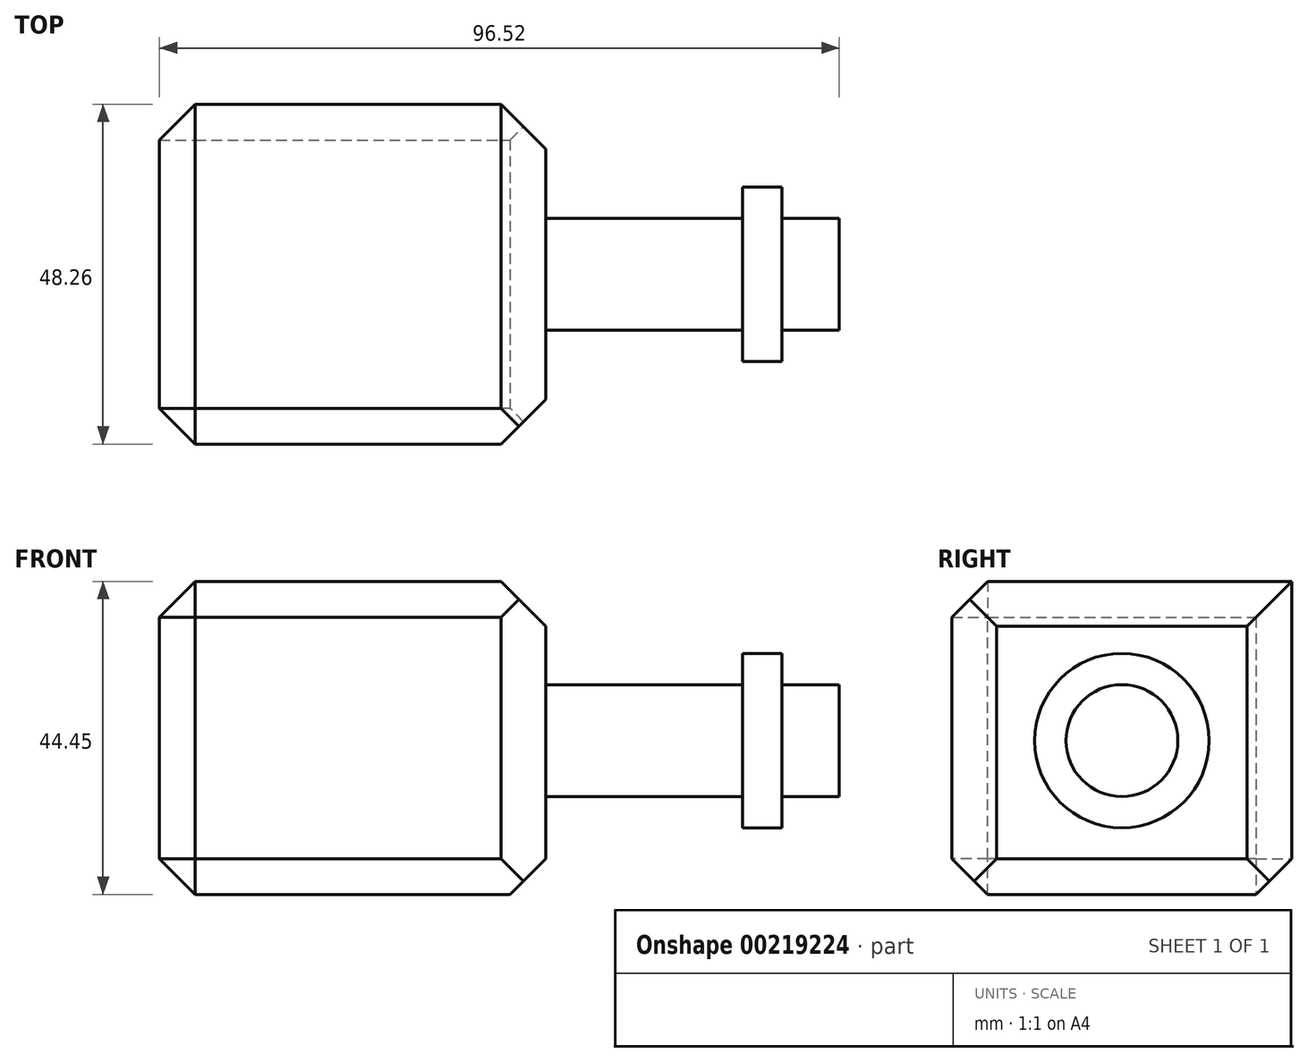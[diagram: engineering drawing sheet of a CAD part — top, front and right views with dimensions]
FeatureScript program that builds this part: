
annotation { "Feature Type Name" : "Feature", "Feature Type Description" : "" }
export const myFeature = defineFeature(function(context is Context, id is Id, definition is map)
    precondition{}
    {
        {
            var Q0;
            Q0=qCreatedBy(makeId("Top.planeOp"),FACE);
            var sketch = newSketch(context, id + "F0", { "sketchPlane" : qUnion([Q0])});
            skLineSegment(sketch, "E0.bottom", {"start": v(-122.1, 35.47) * mm, "end": v(-67.24, 35.47) * mm});
            skLineSegment(sketch, "E0.top", {"start": v(-122.1, -12.8) * mm, "end": v(-67.24, -12.8) * mm});
            skLineSegment(sketch, "E0.left", {"start": v(-122.1, 35.47) * mm, "end": v(-122.1, -12.8) * mm});
            skLineSegment(sketch, "E0.right", {"start": v(-67.24, 35.47) * mm, "end": v(-67.24, -12.8) * mm});
            skSolve(sketch);
        }
        {
            var Q0;
            Q0=makeQuery(id+"F0.imprint","IMPRINT",FACE,{"disambiguationData":[TD([[makeQuery(id+"F0.imprint","IMPRINT",EDGE,{"derivedFrom":sQuery(id+"F0.wireOp",EDGE,"E0.bottom")}),-1.0]])]});
            extrude(context, id + "F1", {"entities" : qUnion([Q0]), "depth" : 44.45 * mm});
        }
        {
            var Q0;
            Q0=makeQuery(id+"F1.opExtrude","SWEPT_FACE",FACE,{"disambiguationData":[OSD([sQuery(id+"F0.wireOp",EDGE,"E0.right")])]});
            var sketch = newSketch(context, id + "F2", { "sketchPlane" : qUnion([Q0])});
            skCircle(sketch, "E1", {"center": v(11.34, 21.84) * mm, "radius": 7.94 * mm});
            skCircle(sketch, "E2", {"center": v(11.34, 21.84) * mm, "radius": 12.39 * mm});
            skSolve(sketch);
        }
        {
            var Q0;
            Q0=makeQuery(id+"F2.imprint","IMPRINT",FACE,{"disambiguationData":[TD([[makeQuery(id+"F2.imprint","IMPRINT",EDGE,{"derivedFrom":sQuery(id+"F2.wireOp",EDGE,"E1")}),1.0]])]});
            extrude(context, id + "F3", {"entities" : qUnion([Q0]), "operationType" : NewBodyOperationType.ADD, "depth" : 41.66 * mm});
        }
        {
            var Q0;
            Q0=makeQuery(id+"F2.imprint","IMPRINT",FACE,{"disambiguationData":[TD([[makeQuery(id+"F2.imprint","IMPRINT",EDGE,{"derivedFrom":sQuery(id+"F2.wireOp",EDGE,"E1")}),-1.0]])]});
            extrude(context, id + "F4", {"entities" : qUnion([Q0]), "operationType" : NewBodyOperationType.ADD, "depth" : 33.53 * mm});
        }
        {
            var Q0;
            Q0=makeQuery(id+"F1.opExtrude","CAP_FACE",FACE,{"disambiguationData":[OSD([sQuery(id+"F0.wireOp",EDGE,"E0.bottom"),sQuery(id+"F0.wireOp",EDGE,"E0.top"),sQuery(id+"F0.wireOp",EDGE,"E0.left"),sQuery(id+"F0.wireOp",EDGE,"E0.right")])],"isStart":false});
            extrude(context, id + "F5", {"entities" : qUnion([Q0]), "operationType" : NewBodyOperationType.REMOVE, "oppositeDirection" : true, "depth" : 36.83 * mm});
        }
        {
            var Q0;
            Q0=makeQuery(id+"F2.imprint","IMPRINT",FACE,{"disambiguationData":[TD([[makeQuery(id+"F2.imprint","IMPRINT",EDGE,{"derivedFrom":sQuery(id+"F2.wireOp",EDGE,"E1")}),-1.0]])]});
            extrude(context, id + "F6", {"entities" : qUnion([Q0]), "operationType" : NewBodyOperationType.REMOVE, "depth" : 27.94 * mm});
        }
        {
            var Q0;
            Q0=makeQuery(id+"F2.imprint","IMPRINT",FACE,{"disambiguationData":[TD([[makeQuery(id+"F2.imprint","IMPRINT",EDGE,{"derivedFrom":sQuery(id+"F2.wireOp",EDGE,"E2")}),-1.0]])]});
            var Q1;
            Q1=makeQuery(id+"F1.opExtrude","SWEPT_FACE",FACE,{"disambiguationData":[OSD([sQuery(id+"F0.wireOp",EDGE,"E0.left")])]});
            extrude(context, id + "F7", {"entities" : qUnion([Q0]), "operationType" : NewBodyOperationType.ADD, "endBound" : BoundingType.UP_TO_SURFACE, "oppositeDirection" : true, "endBoundEntityFace" : qUnion([Q1]), "depth" : 49.02 * mm});
        }
        {
            var Q0;
            Q0=makeQuery(id+"F2.imprint","IMPRINT",FACE,{"disambiguationData":[TD([[makeQuery(id+"F2.imprint","IMPRINT",EDGE,{"derivedFrom":sQuery(id+"F2.wireOp",EDGE,"E1")}),1.0]])]});
            var Q1;
            Q1=makeQuery(id+"F2.imprint","IMPRINT",FACE,{"disambiguationData":[TD([[makeQuery(id+"F2.imprint","IMPRINT",EDGE,{"derivedFrom":sQuery(id+"F2.wireOp",EDGE,"E1")}),-1.0]])]});
            var Q2;
            Q2=makeQuery(id+"F7.boolean.opBoolean","MERGE",FACE,{"derivedFrom":[makeQuery(id+"F1.opExtrude","SWEPT_FACE",FACE,{"disambiguationData":[OSD([sQuery(id+"F0.wireOp",EDGE,"E0.left")])]}),makeQuery(id+"F7.opExtrude","CAP_FACE",FACE,{"disambiguationData":[OSD([sQuery(id+"F0.wireOp",EDGE,"E0.bottom"),sQuery(id+"F0.wireOp",EDGE,"E0.top"),sQuery(id+"F0.wireOp",EDGE,"E0.right"),sQuery(id+"F2.wireOp",EDGE,"E2")])],"isStart":false})]});
            extrude(context, id + "F8", {"entities" : qUnion([Q0, Q1]), "operationType" : NewBodyOperationType.ADD, "endBound" : BoundingType.UP_TO_SURFACE, "oppositeDirection" : true, "endBoundEntityFace" : qUnion([Q2]), "depth" : 103.89 * mm});
        }
        {
            var Q0;
            {var subQ0=sQuery(id+"F0.wireOp",EDGE,"E0.right");Q0=makeQuery(id+"F7.opExtrude","CAP_EDGE",EDGE,{"disambiguationData":[OSD([subQ0]),TDD([makeQuery(id+"F2.imprint","IMPRINT",EDGE,{"derivedFrom":makeQuery(id+"F1.opExtrude","CAP_EDGE",EDGE,{"disambiguationData":[OSD([subQ0])],"isStart":false})})])],"isStart":true});}
            var Q1;
            {var subQ0=sQuery(id+"F0.wireOp",EDGE,"E0.right");var subQ1=sQuery(id+"F0.wireOp",EDGE,"E0.top");Q1=makeQuery(id+"F7.boolean.opBoolean","MERGE",EDGE,{"derivedFrom":[makeQuery(id+"F1.opExtrude","SWEPT_EDGE",EDGE,{"disambiguationData":[OSD([subQ1,subQ0])]}),makeQuery(id+"F7.opExtrude","CAP_EDGE",EDGE,{"disambiguationData":[OSD([subQ1,subQ0])],"isStart":true})]});}
            var Q2;
            {var subQ0=sQuery(id+"F0.wireOp",EDGE,"E0.right");var subQ1=sQuery(id+"F0.wireOp",EDGE,"E0.bottom");Q2=makeQuery(id+"F7.boolean.opBoolean","MERGE",EDGE,{"derivedFrom":[makeQuery(id+"F1.opExtrude","SWEPT_EDGE",EDGE,{"disambiguationData":[OSD([subQ1,subQ0])]}),makeQuery(id+"F7.opExtrude","CAP_EDGE",EDGE,{"disambiguationData":[OSD([subQ1,subQ0])],"isStart":true})]});}
            chamfer(context, id + "F9", {"entities" : qUnion([Q0, Q1, Q2]), "width" : 6.35 * mm, "tangentPropagation" : true});
        }
        {
            var Q0;
            {var subQ0=sQuery(id+"F0.wireOp",EDGE,"E0.right");var subQ1=sQuery(id+"F0.wireOp",EDGE,"E0.top");Q0=makeQuery(id+"F7.opExtrude","SWEPT_EDGE",EDGE,{"disambiguationData":[OSD([subQ1,subQ0]),TDD([makeQuery(id+"F2.imprint","INTERSECT",VERTEX,{"derivedFrom":[makeQuery(id+"F1.opExtrude","SWEPT_EDGE",EDGE,{"disambiguationData":[OSD([subQ1,subQ0])]}),makeQuery(id+"F1.opExtrude","CAP_EDGE",EDGE,{"disambiguationData":[OSD([subQ0])],"isStart":false})]})])]});}
            var Q1;
            {var subQ0=sQuery(id+"F0.wireOp",EDGE,"E0.top");Q1=makeQuery(id+"F7.boolean.opBoolean","MERGE",EDGE,{"derivedFrom":[makeQuery(id+"F1.opExtrude","SWEPT_EDGE",EDGE,{"disambiguationData":[OSD([subQ0,sQuery(id+"F0.wireOp",EDGE,"E0.left")])]}),makeQuery(id+"F7.opExtrude","CAP_EDGE",EDGE,{"disambiguationData":[OSD([subQ0,sQuery(id+"F0.wireOp",EDGE,"E0.right")])],"isStart":false})]});}
            var Q2;
            {var subQ0=sQuery(id+"F0.wireOp",EDGE,"E0.right");Q2=makeQuery(id+"F7.opExtrude","CAP_EDGE",EDGE,{"disambiguationData":[OSD([subQ0]),TDD([makeQuery(id+"F2.imprint","IMPRINT",EDGE,{"derivedFrom":makeQuery(id+"F1.opExtrude","CAP_EDGE",EDGE,{"disambiguationData":[OSD([subQ0])],"isStart":false})})])],"isStart":false});}
            var Q3;
            {var subQ0=sQuery(id+"F0.wireOp",EDGE,"E0.bottom");Q3=makeQuery(id+"F7.boolean.opBoolean","MERGE",EDGE,{"derivedFrom":[makeQuery(id+"F1.opExtrude","SWEPT_EDGE",EDGE,{"disambiguationData":[OSD([subQ0,sQuery(id+"F0.wireOp",EDGE,"E0.left")])]}),makeQuery(id+"F7.opExtrude","CAP_EDGE",EDGE,{"disambiguationData":[OSD([subQ0,sQuery(id+"F0.wireOp",EDGE,"E0.right")])],"isStart":false})]});}
            var Q4;
            Q4=makeQuery(id+"F1.opExtrude","CAP_EDGE",EDGE,{"disambiguationData":[OSD([sQuery(id+"F0.wireOp",EDGE,"E0.top")])],"isStart":true});
            var Q5;
            Q5=makeQuery(id+"F1.opExtrude","CAP_EDGE",EDGE,{"disambiguationData":[OSD([sQuery(id+"F0.wireOp",EDGE,"E0.bottom")])],"isStart":true});
            var Q6;
            Q6=makeQuery(id+"F1.opExtrude","CAP_EDGE",EDGE,{"disambiguationData":[OSD([sQuery(id+"F0.wireOp",EDGE,"E0.right")])],"isStart":true});
            var Q7;
            Q7=makeQuery(id+"F1.opExtrude","CAP_EDGE",EDGE,{"disambiguationData":[OSD([sQuery(id+"F0.wireOp",EDGE,"E0.left")])],"isStart":true});
            chamfer(context, id + "F10", {"entities" : qUnion([Q0, Q1, Q2, Q3, Q4, Q5, Q6, Q7]), "width" : 5.08 * mm, "tangentPropagation" : true});
        }
    });
